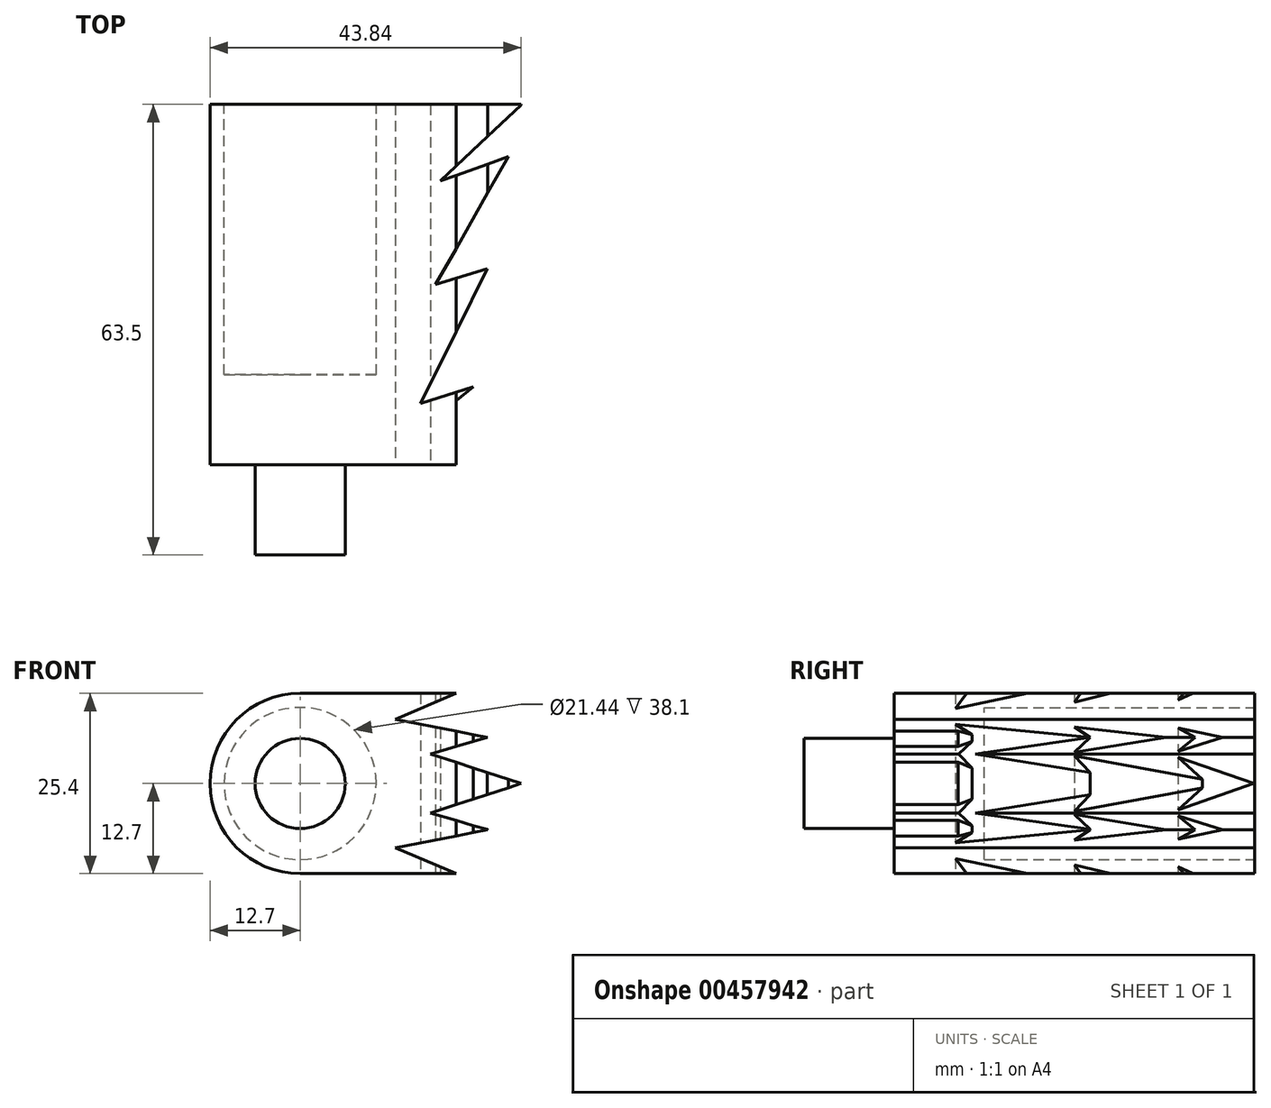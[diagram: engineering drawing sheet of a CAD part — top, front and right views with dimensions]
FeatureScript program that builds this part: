
annotation { "Feature Type Name" : "Feature", "Feature Type Description" : "" }
export const myFeature = defineFeature(function(context is Context, id is Id, definition is map)
    precondition{}
    {
        {
            var Q0;
            Q0=qCreatedBy(makeId("Front.planeOp"),FACE);
            var sketch = newSketch(context, id + "F0", { "sketchPlane" : qUnion([Q0])});
            skCircle(sketch, "E0", {"center": v(0, 0) * mm, "radius": 10.72 * mm});
            skCircle(sketch, "E1", {"center": v(0, 0) * mm, "radius": 12.7 * mm});
            skSolve(sketch);
        }
        {
            var Q0;
            Q0 = qSketchRegion(id + "F0", true);
            var Q1;
            Q1=makeQuery(id+"F0.imprint","IMPRINT",FACE,{"disambiguationData":[TD([[makeQuery(id+"F0.imprint","IMPRINT",EDGE,{"derivedFrom":sQuery(id+"F0.wireOp",EDGE,"E0")}),1.0]])]});
            extrude(context, id + "F1", {"entities" : qUnion([Q0, Q1]), "depth" : 50.8 * mm, "offsetDistance" : 25.4 * mm});
        }
        {
            var Q0;
            Q0=makeQuery(id+"F0.imprint","IMPRINT",FACE,{"disambiguationData":[TD([[makeQuery(id+"F0.imprint","IMPRINT",EDGE,{"derivedFrom":sQuery(id+"F0.wireOp",EDGE,"E0")}),1.0]])]});
            extrude(context, id + "F2", {"entities" : qUnion([Q0]), "operationType" : NewBodyOperationType.REMOVE, "depth" : 38.1 * mm, "offsetDistance" : 25.4 * mm});
        }
        {
            var Q0;
            Q0=makeQuery(id+"F1.opExtrude","CAP_FACE",FACE,{"disambiguationData":[OSD([sQuery(id+"F0.wireOp",EDGE,"E1")])],"isStart":false});
            var sketch = newSketch(context, id + "F3", { "sketchPlane" : qUnion([Q0])});
            skLineSegment(sketch, "E2", {"start": v(0, -12.7) * mm, "end": v(21.96, -12.7) * mm});
            skLineSegment(sketch, "E3", {"start": v(21.96, -12.7) * mm, "end": v(13.43, -9.07) * mm});
            skLineSegment(sketch, "E4", {"start": v(13.43, -9.07) * mm, "end": v(26.44, -6.5) * mm});
            skLineSegment(sketch, "E5", {"start": v(26.44, -6.5) * mm, "end": v(18.33, -4.16) * mm});
            skLineSegment(sketch, "E6", {"start": v(18.33, -4.16) * mm, "end": v(31.14, 0) * mm});
            skLineSegment(sketch, "E7", {"start": v(31.14, 0) * mm, "end": v(0, 0) * mm});
            skArc(sketch, "E8", {"start": v(0, -12.7) * mm, "mid": v(8.98, -8.98) * mm, "end": v(12.7, 0) * mm});
            skArc(sketch, "E9.MirrorCS", {"start": v(0, 12.7) * mm, "mid": v(8.98, 8.98) * mm, "end": v(12.7, 0) * mm});
            skLineSegment(sketch, "E10.MirrorCS", {"start": v(0, 12.7) * mm, "end": v(21.96, 12.7) * mm});
            skLineSegment(sketch, "E11.MirrorCS", {"start": v(21.96, 12.7) * mm, "end": v(13.43, 9.07) * mm});
            skLineSegment(sketch, "E12.MirrorCS", {"start": v(13.43, 9.07) * mm, "end": v(26.44, 6.5) * mm});
            skLineSegment(sketch, "E13.MirrorCS", {"start": v(26.44, 6.5) * mm, "end": v(18.33, 4.16) * mm});
            skLineSegment(sketch, "E14.MirrorCS", {"start": v(18.33, 4.16) * mm, "end": v(31.14, 0) * mm});
            skSolve(sketch);
        }
        {
            var Q0;
            Q0=makeQuery(id+"F3.imprint","IMPRINT",FACE,{"disambiguationData":[TD([[makeQuery(id+"F3.imprint","IMPRINT",EDGE,{"derivedFrom":sQuery(id+"F3.wireOp",EDGE,"E2")}),1.0]])]});
            var Q1;
            {var subQ0=sQuery(id+"F3.wireOp",EDGE,"E9.MirrorCS");Q1=makeQuery(id+"F3.imprint","IMPRINT",FACE,{"disambiguationData":[TD([[makeQuery(id+"F3.imprint","IMPRINT",EDGE,{"derivedFrom":subQ0}),-1.0]])]});}
            extrude(context, id + "F4", {"entities" : qUnion([Q0, Q1]), "operationType" : NewBodyOperationType.ADD, "oppositeDirection" : true, "depth" : 50.8 * mm, "offsetDistance" : 25.4 * mm});
        }
        {
            var Q0;
            Q0=makeQuery(id+"F4.opExtrude","SWEPT_FACE",FACE,{"disambiguationData":[OSD([sQuery(id+"F3.wireOp",EDGE,"E2")])]});
            var sketch = newSketch(context, id + "F5", { "sketchPlane" : qUnion([Q0])});
            skLineSegment(sketch, "E15.0", {"start": v(-10.72, 0) * mm, "end": v(10.72, 0) * mm});
            skLineSegment(sketch, "E16", {"start": v(10.72, 0) * mm, "end": v(10.72, 50.8) * mm});
            skLineSegment(sketch, "E17", {"start": v(10.72, 50.8) * mm, "end": v(24.42, 39.8) * mm});
            skLineSegment(sketch, "E18", {"start": v(24.42, 39.8) * mm, "end": v(16.96, 42.15) * mm});
            skLineSegment(sketch, "E19", {"start": v(16.96, 42.15) * mm, "end": v(26.34, 23.16) * mm});
            skLineSegment(sketch, "E20", {"start": v(26.34, 23.16) * mm, "end": v(19.09, 25.4) * mm});
            skPoint(sketch, "E20.endSnap0", {"position": v(21.96, 25.4) * mm});
            skLineSegment(sketch, "E21", {"start": v(19.09, 25.4) * mm, "end": v(29.33, 7.37) * mm});
            skLineSegment(sketch, "E22", {"start": v(29.33, 7.37) * mm, "end": v(19.73, 10.78) * mm});
            skLineSegment(sketch, "E23", {"start": v(19.73, 10.78) * mm, "end": v(31.25, 0) * mm});
            skLineSegment(sketch, "E24", {"start": v(10.72, 50.8) * mm, "end": v(46.69, 21.93) * mm});
            skLineSegment(sketch, "E25", {"start": v(46.69, 21.93) * mm, "end": v(46.69, 50.8) * mm});
            skLineSegment(sketch, "E26", {"start": v(46.69, 50.8) * mm, "end": v(10.72, 50.8) * mm});
            skLineSegment(sketch, "E27", {"start": v(46.69, 21.93) * mm, "end": v(46.69, 0) * mm});
            skLineSegment(sketch, "E28", {"start": v(46.69, 0) * mm, "end": v(31.25, 0) * mm});
            skSolve(sketch);
        }
        {
            var Q0;
            {var subQ3=sQuery(id+"F5.wireOp",EDGE,"E25");Q0=makeQuery(id+"F5.imprint","IMPRINT",FACE,{"disambiguationData":[TD([[makeQuery(id+"F5.imprint","IMPRINT",EDGE,{"derivedFrom":subQ3}),1.0]])]});}
            var Q1;
            {var subQ1=sQuery(id+"F5.wireOp",EDGE,"E24");var subQ2=sQuery(id+"F3.wireOp",EDGE,"E2");var subQ4=makeQuery(id+"F4.opExtrude","SWEPT_EDGE",EDGE,{"disambiguationData":[OSD([subQ2,sQuery(id+"F3.wireOp",EDGE,"E3")])]});var subQ5=makeQuery(id+"F5.imprint","INTERSECT",VERTEX,{"derivedFrom":[subQ4,subQ1]});Q1=makeQuery(id+"F5.imprint","IMPRINT",FACE,{"disambiguationData":[TD([[makeQuery(id+"F5.imprint","IMPRINT",EDGE,{"disambiguationData":[TD([[subQ5,1.0]])],"derivedFrom":subQ1}),1.0]])]});}
            var Q2;
            {var subQ12=sQuery(id+"F5.wireOp",EDGE,"E27");Q2=makeQuery(id+"F5.imprint","IMPRINT",FACE,{"disambiguationData":[TD([[makeQuery(id+"F5.imprint","IMPRINT",EDGE,{"derivedFrom":subQ12}),-1.0]])]});}
            var Q3;
            {var subQ0=sQuery(id+"F5.wireOp",EDGE,"E19");var subQ1=sQuery(id+"F5.wireOp",EDGE,"E18");var subQ2=makeQuery(id+"F5.imprint","INTERSECT",VERTEX,{"derivedFrom":[subQ1,subQ0]});Q3=makeQuery(id+"F5.imprint","IMPRINT",FACE,{"disambiguationData":[TD([[makeQuery(id+"F5.imprint","IMPRINT",EDGE,{"disambiguationData":[TD([[subQ2,1.0]])],"derivedFrom":subQ1}),1.0]])]});}
            var Q4;
            {var subQ0=sQuery(id+"F5.wireOp",EDGE,"E21");var subQ1=sQuery(id+"F5.wireOp",EDGE,"E20");var subQ2=makeQuery(id+"F5.imprint","INTERSECT",VERTEX,{"derivedFrom":[subQ1,subQ0]});Q4=makeQuery(id+"F5.imprint","IMPRINT",FACE,{"disambiguationData":[TD([[makeQuery(id+"F5.imprint","IMPRINT",EDGE,{"disambiguationData":[TD([[subQ2,1.0]])],"derivedFrom":subQ1}),1.0]])]});}
            var Q5;
            {var subQ0=sQuery(id+"F5.wireOp",EDGE,"E23");var subQ1=sQuery(id+"F5.wireOp",EDGE,"E22");var subQ2=makeQuery(id+"F5.imprint","INTERSECT",VERTEX,{"derivedFrom":[subQ1,subQ0]});Q5=makeQuery(id+"F5.imprint","IMPRINT",FACE,{"disambiguationData":[TD([[makeQuery(id+"F5.imprint","IMPRINT",EDGE,{"disambiguationData":[TD([[subQ2,1.0]])],"derivedFrom":subQ1}),1.0]])]});}
            extrude(context, id + "F6", {"entities" : qUnion([Q0, Q1, Q2, Q3, Q4, Q5]), "operationType" : NewBodyOperationType.REMOVE, "oppositeDirection" : true, "depth" : 81.8 * mm, "offsetDistance" : 25.4 * mm});
        }
        {
            var Q0;
            Q0=makeQuery(id+"F4.boolean.opBoolean","MERGE",FACE,{"derivedFrom":[makeQuery(id+"F1.opExtrude","CAP_FACE",FACE,{"disambiguationData":[OSD([sQuery(id+"F0.wireOp",EDGE,"E1")])],"isStart":false}),makeQuery(id+"F4.opExtrude","CAP_FACE",FACE,{"disambiguationData":[OSD([sQuery(id+"F3.wireOp",EDGE,"E2"),sQuery(id+"F3.wireOp",EDGE,"E3"),sQuery(id+"F3.wireOp",EDGE,"E4"),sQuery(id+"F3.wireOp",EDGE,"E5"),sQuery(id+"F3.wireOp",EDGE,"E6"),sQuery(id+"F3.wireOp",EDGE,"E8"),sQuery(id+"F3.wireOp",EDGE,"E9.MirrorCS"),sQuery(id+"F3.wireOp",EDGE,"E10.MirrorCS"),sQuery(id+"F3.wireOp",EDGE,"E11.MirrorCS"),sQuery(id+"F3.wireOp",EDGE,"E12.MirrorCS"),sQuery(id+"F3.wireOp",EDGE,"E13.MirrorCS"),sQuery(id+"F3.wireOp",EDGE,"E14.MirrorCS")])],"isStart":true})]});
            var sketch = newSketch(context, id + "F7", { "sketchPlane" : qUnion([Q0])});
            skCircle(sketch, "E29", {"center": v(0, 0) * mm, "radius": 6.35 * mm});
            skSolve(sketch);
        }
        {
            var Q0;
            Q0 = qSketchRegion(id + "F7", true);
            extrude(context, id + "F8", {"entities" : qUnion([Q0]), "operationType" : NewBodyOperationType.ADD, "depth" : 12.7 * mm, "offsetDistance" : 25.4 * mm});
        }
    });
